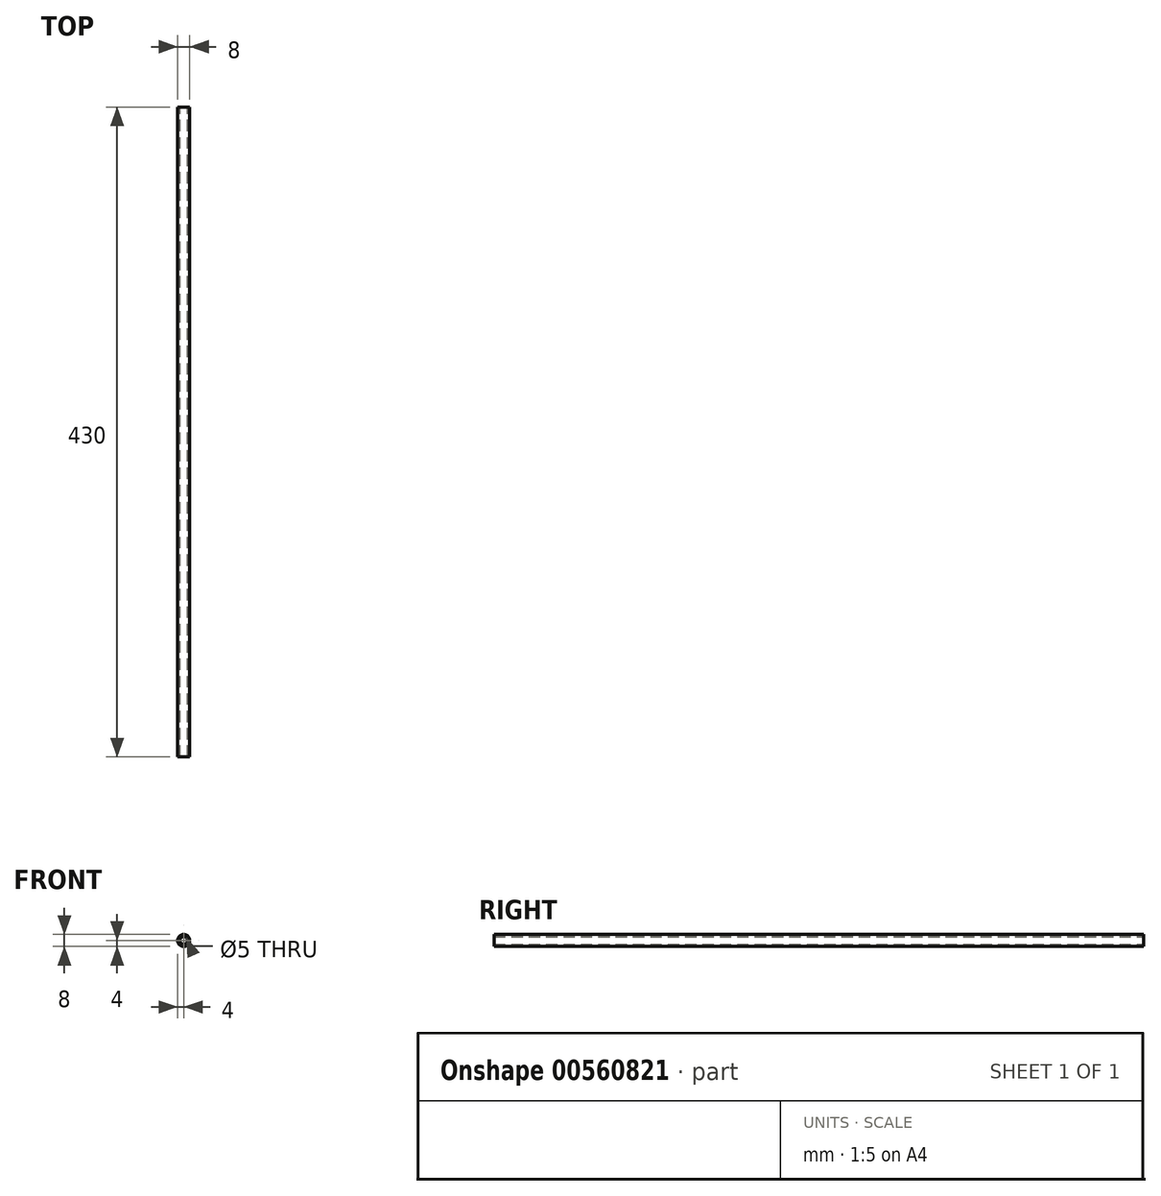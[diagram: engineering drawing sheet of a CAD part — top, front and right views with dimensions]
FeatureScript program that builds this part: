
annotation { "Feature Type Name" : "Feature", "Feature Type Description" : "" }
export const myFeature = defineFeature(function(context is Context, id is Id, definition is map)
    precondition{}
    {
        {
            var Q0;
            Q0=qCreatedBy(makeId("Front.planeOp"),FACE);
            var sketch = newSketch(context, id + "F0", { "sketchPlane" : qUnion([Q0])});
            skCircle(sketch, "E0", {"center": v(0, 0) * mm, "radius": 4 * mm});
            skCircle(sketch, "E1", {"center": v(0, 0) * mm, "radius": 2.5 * mm});
            skSolve(sketch);
        }
        {
            var Q0;
            Q0=qSketchRegion(id+"F0",true);
            extrude(context, id + "F1", {"entities" : qUnion([Q0]), "endBound" : BoundingType.SYMMETRIC, "depth" : 430 * mm, "offsetDistance" : 25 * mm});
        }
    });
